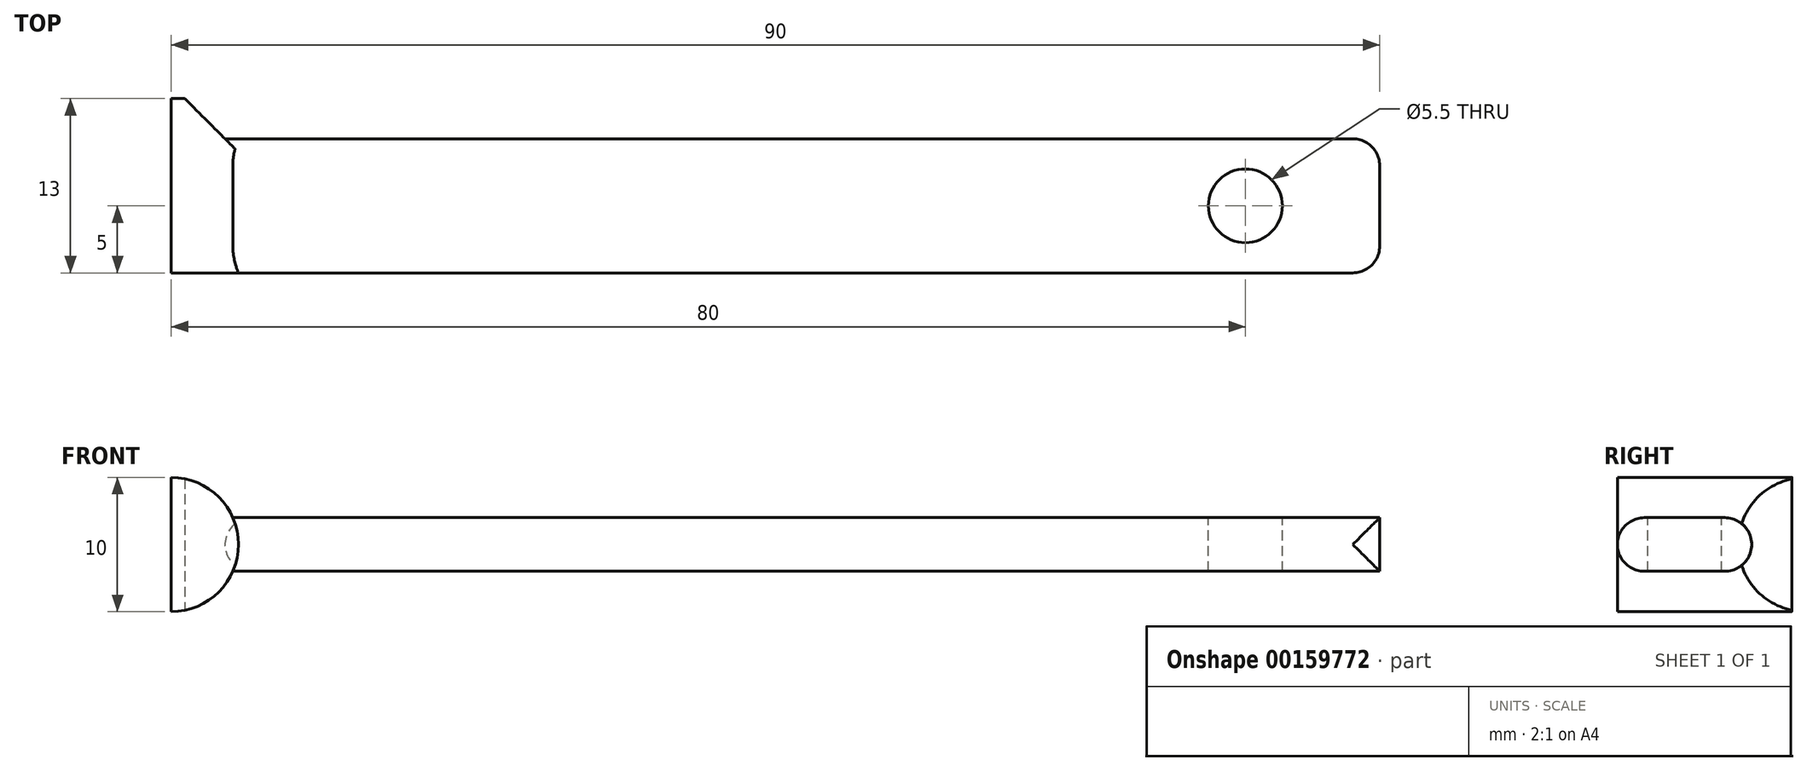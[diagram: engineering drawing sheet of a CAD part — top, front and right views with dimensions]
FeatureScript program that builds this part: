
annotation { "Feature Type Name" : "Feature", "Feature Type Description" : "" }
export const myFeature = defineFeature(function(context is Context, id is Id, definition is map)
    precondition{}
    {
        {
            var Q0;
            Q0=qCreatedBy(makeId("Top.planeOp"),FACE);
            var sketch = newSketch(context, id + "F0", { "sketchPlane" : qUnion([Q0])});
            skLineSegment(sketch, "E0.bottom", {"start": v(45, -5) * mm, "end": v(-45, -5) * mm});
            skLineSegment(sketch, "E0.top", {"start": v(45, 5) * mm, "end": v(-45, 5) * mm});
            skLineSegment(sketch, "E0.left", {"start": v(45, -5) * mm, "end": v(45, 5) * mm});
            skLineSegment(sketch, "E0.right", {"start": v(-45, -5) * mm, "end": v(-45, 5) * mm});
            skPoint(sketch, "E0.middle", {"position": v(0, 0) * mm});
            skSolve(sketch);
        }
        {
            var Q0;
            Q0=makeQuery(id+"F0.imprint","IMPRINT",FACE,{"disambiguationData":[TD([[makeQuery(id+"F0.imprint","IMPRINT",EDGE,{"derivedFrom":sQuery(id+"F0.wireOp",EDGE,"E0.bottom")}),-1.0]])]});
            extrude(context, id + "F1", {"entities" : qUnion([Q0]), "depth" : 2 * mm});
        }
        {
            var Q0;
            Q0=makeQuery(id+"F1.opExtrude","CAP_FACE",FACE,{"disambiguationData":[OSD([sQuery(id+"F0.wireOp",EDGE,"E0.bottom"),sQuery(id+"F0.wireOp",EDGE,"E0.top"),sQuery(id+"F0.wireOp",EDGE,"E0.left"),sQuery(id+"F0.wireOp",EDGE,"E0.right")])],"isStart":false});
            var sketch = newSketch(context, id + "F2", { "sketchPlane" : qUnion([Q0])});
            skLineSegment(sketch, "E1.bottom", {"start": v(-45, 5) * mm, "end": v(-40, 5) * mm});
            skLineSegment(sketch, "E1.top", {"start": v(-45, -5) * mm, "end": v(-40, -5) * mm});
            skLineSegment(sketch, "E1.left", {"start": v(-45, 5) * mm, "end": v(-45, -5) * mm});
            skLineSegment(sketch, "E1.right", {"start": v(-40, 5) * mm, "end": v(-40, -5) * mm});
            skSolve(sketch);
        }
        {
            var Q0;
            Q0=makeQuery(id+"F2.imprint","IMPRINT",FACE,{"disambiguationData":[TD([[makeQuery(id+"F2.imprint","IMPRINT",EDGE,{"derivedFrom":sQuery(id+"F2.wireOp",EDGE,"E1.bottom")}),1.0]])]});
            extrude(context, id + "F3", {"entities" : qUnion([Q0]), "operationType" : NewBodyOperationType.ADD, "depth" : 3 * mm});
        }
        {
            var Q0;
            Q0=makeQuery(id+"F1.opExtrude","SWEPT_BODY",BODY,{"disambiguationData":[OSD([sQuery(id+"F0.wireOp",EDGE,"E0.bottom"),sQuery(id+"F0.wireOp",EDGE,"E0.top"),sQuery(id+"F0.wireOp",EDGE,"E0.left"),sQuery(id+"F0.wireOp",EDGE,"E0.right")])]});
            var Q1;
            Q1=qCreatedBy(makeId("Top.planeOp"),FACE);
            mirror(context, id + "F4", {"operationType" : NewBodyOperationType.ADD, "entities" : qUnion([Q0]), "mirrorPlane" : qUnion([Q1])});
        }
        {
            var Q0;
            Q0=makeQuery(id+"F1.opExtrude","CAP_FACE",FACE,{"disambiguationData":[OSD([sQuery(id+"F0.wireOp",EDGE,"E0.bottom"),sQuery(id+"F0.wireOp",EDGE,"E0.top"),sQuery(id+"F0.wireOp",EDGE,"E0.left"),sQuery(id+"F0.wireOp",EDGE,"E0.right")])],"isStart":false});
            var sketch = newSketch(context, id + "F5", { "sketchPlane" : qUnion([Q0])});
            skPoint(sketch, "E2", {"position": v(35, 0) * mm});
            skPoint(sketch, "E2.positionSnap0", {"position": v(45, 0) * mm});
            skSolve(sketch);
        }
        {
            var Q0;
            Q0=sQuery(id+"F5.wireOp",VERTEX,"E2");
            var Q1;
            Q1=makeQuery(id+"F1.opExtrude","SWEPT_BODY",BODY,{"disambiguationData":[OSD([sQuery(id+"F0.wireOp",EDGE,"E0.bottom"),sQuery(id+"F0.wireOp",EDGE,"E0.top"),sQuery(id+"F0.wireOp",EDGE,"E0.left"),sQuery(id+"F0.wireOp",EDGE,"E0.right")])]});
            hole(context, id + "F6", {"style" : HoleStyle.SIMPLE, "endStyle" : HoleEndStyle.THROUGH, "holeDiameter" : 5.5 * mm, "locations" : qUnion([Q0]), "scope" : qUnion([Q1]), "isTappedThrough" : true});
        }
        {
            var Q0;
            {var subQ0=makeQuery(id+"F3.boolean.opBoolean","MERGE",FACE,{"derivedFrom":[makeQuery(id+"F1.opExtrude","SWEPT_FACE",FACE,{"disambiguationData":[OSD([sQuery(id+"F0.wireOp",EDGE,"E0.top")])]}),makeQuery(id+"F3.opExtrude","SWEPT_FACE",FACE,{"disambiguationData":[OSD([sQuery(id+"F2.wireOp",EDGE,"E1.bottom")])]})]});Q0=makeQuery(id+"F4.boolean.opBoolean","MERGE",FACE,{"derivedFrom":[subQ0,makeQuery(id+"F4.opPattern","COPY",FACE,{"derivedFrom":subQ0,"instanceName":"1"})]});}
            var sketch = newSketch(context, id + "F7", { "sketchPlane" : qUnion([Q0])});
            skLineSegment(sketch, "E3.bottom", {"start": v(45, -5) * mm, "end": v(40, -5) * mm});
            skLineSegment(sketch, "E3.top", {"start": v(45, 5) * mm, "end": v(40, 5) * mm});
            skLineSegment(sketch, "E3.left", {"start": v(45, -5) * mm, "end": v(45, 5) * mm});
            skLineSegment(sketch, "E3.right", {"start": v(40, -5) * mm, "end": v(40, 5) * mm});
            skSolve(sketch);
        }
        {
            var Q0;
            {var subQ5=sQuery(id+"F7.wireOp",EDGE,"E3.bottom");Q0=makeQuery(id+"F7.imprint","IMPRINT",FACE,{"disambiguationData":[TD([[makeQuery(id+"F7.imprint","IMPRINT",EDGE,{"derivedFrom":subQ5}),1.0]])]});}
            extrude(context, id + "F8", {"entities" : qUnion([Q0]), "operationType" : NewBodyOperationType.ADD, "depth" : 3 * mm});
        }
        {
            var Q0;
            Q0=makeQuery(id+"F8.opExtrude","CAP_EDGE",EDGE,{"disambiguationData":[OSD([sQuery(id+"F7.wireOp",EDGE,"E3.right")])],"isStart":false});
            chamfer(context, id + "F9", {"entities" : qUnion([Q0]), "width" : 4 * mm, "tangentPropagation" : true});
        }
        {
            var Q0;
            {var subQ0=makeQuery(id+"F1.opExtrude","SWEPT_EDGE",EDGE,{"disambiguationData":[OSD([sQuery(id+"F0.wireOp",EDGE,"E0.top"),sQuery(id+"F0.wireOp",EDGE,"E0.left")])]});Q0=makeQuery(id+"F4.boolean.opBoolean","MERGE",EDGE,{"derivedFrom":[subQ0,makeQuery(id+"F4.opPattern","COPY",EDGE,{"derivedFrom":subQ0,"instanceName":"1"})]});}
            var Q1;
            {var subQ0=makeQuery(id+"F1.opExtrude","SWEPT_EDGE",EDGE,{"disambiguationData":[OSD([sQuery(id+"F0.wireOp",EDGE,"E0.bottom"),sQuery(id+"F0.wireOp",EDGE,"E0.left")])]});Q1=makeQuery(id+"F4.boolean.opBoolean","MERGE",EDGE,{"derivedFrom":[subQ0,makeQuery(id+"F4.opPattern","COPY",EDGE,{"derivedFrom":subQ0,"instanceName":"1"})]});}
            var Q2;
            Q2=makeQuery(id+"F1.opExtrude","CAP_EDGE",EDGE,{"disambiguationData":[OSD([sQuery(id+"F0.wireOp",EDGE,"E0.bottom")])],"isStart":false});
            var Q3;
            Q3=makeQuery(id+"F1.opExtrude","CAP_EDGE",EDGE,{"disambiguationData":[OSD([sQuery(id+"F0.wireOp",EDGE,"E0.top")])],"isStart":false});
            var Q4;
            Q4=makeQuery(id+"F4.opPattern","COPY",EDGE,{"derivedFrom":makeQuery(id+"F1.opExtrude","CAP_EDGE",EDGE,{"disambiguationData":[OSD([sQuery(id+"F0.wireOp",EDGE,"E0.top")])],"isStart":false}),"instanceName":"1"});
            var Q5;
            Q5=makeQuery(id+"F4.opPattern","COPY",EDGE,{"derivedFrom":makeQuery(id+"F1.opExtrude","CAP_EDGE",EDGE,{"disambiguationData":[OSD([sQuery(id+"F0.wireOp",EDGE,"E0.bottom")])],"isStart":false}),"instanceName":"1"});
            fillet(context, id + "F10", {"entities" : qUnion([Q0, Q1, Q2, Q3, Q4, Q5]), "radius" : 2 * mm, "tangentPropagation" : true, "allowEdgeOverflow" : false});
        }
        {
            var Q0;
            Q0=makeQuery(id+"F8.boolean.opBoolean","MERGE",EDGE,{"derivedFrom":[makeQuery(id+"F3.opExtrude","CAP_EDGE",EDGE,{"disambiguationData":[OSD([sQuery(id+"F2.wireOp",EDGE,"E1.right")])],"isStart":false}),makeQuery(id+"F8.opExtrude","SWEPT_EDGE",EDGE,{"disambiguationData":[OSD([sQuery(id+"F7.wireOp",EDGE,"E3.top"),sQuery(id+"F7.wireOp",EDGE,"E3.right")])]})]});
            var Q1;
            Q1=makeQuery(id+"F8.boolean.opBoolean","MERGE",EDGE,{"derivedFrom":[makeQuery(id+"F4.opPattern","COPY",EDGE,{"derivedFrom":makeQuery(id+"F3.opExtrude","CAP_EDGE",EDGE,{"disambiguationData":[OSD([sQuery(id+"F2.wireOp",EDGE,"E1.right")])],"isStart":false}),"instanceName":"1"}),makeQuery(id+"F8.opExtrude","SWEPT_EDGE",EDGE,{"disambiguationData":[OSD([sQuery(id+"F7.wireOp",EDGE,"E3.bottom"),sQuery(id+"F7.wireOp",EDGE,"E3.right")])]})]});
            fillet(context, id + "F11", {"entities" : qUnion([Q0, Q1]), "radius" : 5 * mm, "tangentPropagation" : true, "allowEdgeOverflow" : false});
        }
    });
